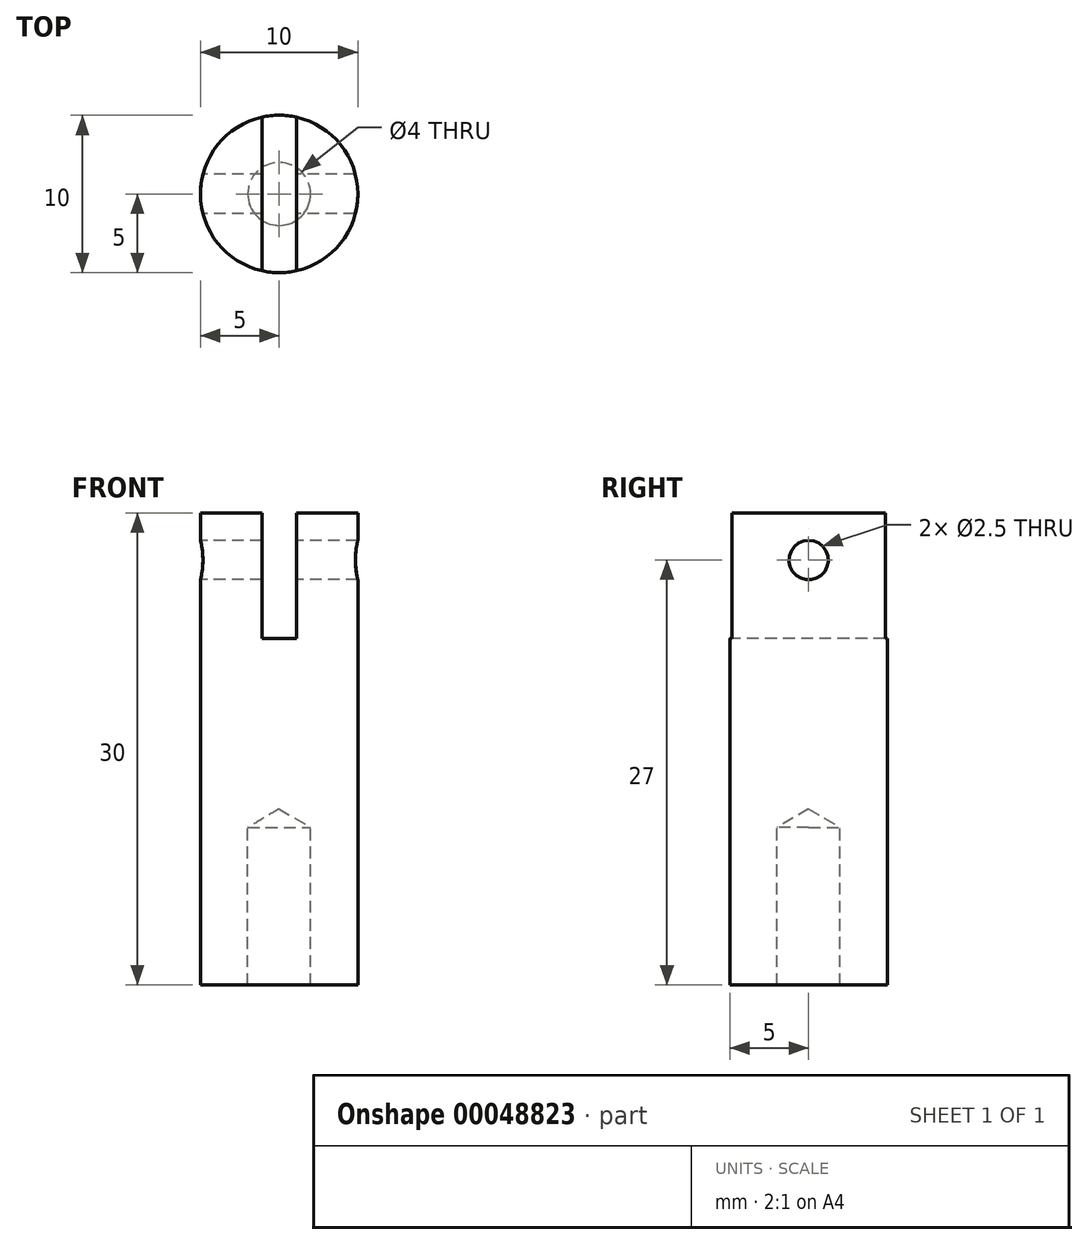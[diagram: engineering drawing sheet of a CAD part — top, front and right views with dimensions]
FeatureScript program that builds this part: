
annotation { "Feature Type Name" : "Feature", "Feature Type Description" : "" }
export const myFeature = defineFeature(function(context is Context, id is Id, definition is map)
    precondition{}
    {
        {
            var Q0;
            Q0=qCreatedBy(makeId("Top.planeOp"),FACE);
            var sketch = newSketch(context, id + "F0", { "sketchPlane" : qUnion([Q0])});
            skCircle(sketch, "E0", {"center": v(0, 0) * mm, "radius": 5 * mm});
            skSolve(sketch);
        }
        {
            var Q0;
            Q0 = qSketchRegion(id + "F0", true);
            extrude(context, id + "F1", {"entities" : qUnion([Q0]), "depth" : 30 * mm});
        }
        {
            var Q0;
            Q0=makeQuery(id+"F1.opExtrude","CAP_FACE",FACE,{"disambiguationData":[OSD([sQuery(id+"F0.wireOp",EDGE,"E0")])],"isStart":false});
            var sketch = newSketch(context, id + "F2", { "sketchPlane" : qUnion([Q0])});
            skLineSegment(sketch, "E1", {"start": v(-1.1, 4.88) * mm, "end": v(-1.1, -4.88) * mm, "construction": true});
            skLineSegment(sketch, "E2.MirrorCS", {"start": v(1.1, 4.88) * mm, "end": v(1.1, -4.88) * mm, "construction": true});
            skLineSegment(sketch, "E3", {"start": v(-1.1, 4.88) * mm, "end": v(-1.1, -4.88) * mm});
            skLineSegment(sketch, "E4", {"start": v(1.1, 4.88) * mm, "end": v(1.1, -4.88) * mm});
            skSolve(sketch);
        }
        {
            var Q0;
            {var subQ0=sQuery(id+"F2.wireOp",EDGE,"E3");Q0=makeQuery(id+"F2.imprint","IMPRINT",FACE,{"disambiguationData":[TD([[makeQuery(id+"F2.imprint","IMPRINT",EDGE,{"derivedFrom":subQ0}),1.0]])]});}
            extrude(context, id + "F3", {"entities" : qUnion([Q0]), "operationType" : NewBodyOperationType.REMOVE, "oppositeDirection" : true, "depth" : 8 * mm});
        }
        {
            var Q0;
            Q0=qCreatedBy(makeId("Right.planeOp"),FACE);
            var sketch = newSketch(context, id + "F4", { "sketchPlane" : qUnion([Q0])});
            skPoint(sketch, "E5", {"position": v(0, 27) * mm});
            skCircle(sketch, "E6", {"center": v(0, 27) * mm, "radius": 1.25 * mm});
            skSolve(sketch);
        }
        {
            var Q0;
            Q0=makeQuery(id+"F4.imprint","IMPRINT",FACE,{"disambiguationData":[TD([[makeQuery(id+"F4.imprint","IMPRINT",EDGE,{"derivedFrom":sQuery(id+"F4.wireOp",EDGE,"E6")}),1.0]])]});
            var Q1;
            Q1=sQuery(id+"F4.wireOp",EDGE,"E6");
            extrude(context, id + "F5", {"entities" : qUnion([Q0]), "operationType" : NewBodyOperationType.REMOVE, "surfaceEntities" : qUnion([Q1]), "depth" : 10 * mm, "symmetric" : true});
        }
        {
            var Q0;
            Q0=makeQuery(id+"F1.opExtrude","CAP_FACE",FACE,{"disambiguationData":[OSD([sQuery(id+"F0.wireOp",EDGE,"E0")])],"isStart":true});
            var sketch = newSketch(context, id + "F6", { "sketchPlane" : qUnion([Q0])});
            skPoint(sketch, "E7", {"position": v(0, 0) * mm});
            skSolve(sketch);
        }
        {
            var Q0;
            Q0=sQuery(id+"F6.wireOp",VERTEX,"E7");
            var Q1;
            Q1=makeQuery(id+"F1.opExtrude","SWEPT_BODY",BODY,{"disambiguationData":[OSD([sQuery(id+"F0.wireOp",EDGE,"E0")])]});
            hole(context, id + "F7", {"style" : HoleStyle.SIMPLE, "endStyle" : HoleEndStyle.BLIND, "standardTappedOrClearance" : lookupTablePath({ "standard" : "ISO", "engagement" : "75%", "pitch" : "1 mm", "size" : "M5", "type" : "Tapped" }), "standardBlindInLast" : lookupTablePath({ "standard" : "ISO", "engagement" : "75%", "pitch" : "1 mm", "size" : "M5", "type" : "Tapped" }), "holeDiameter" : 4 * mm, "holeDepth" : 10 * mm, "locations" : qUnion([Q0]), "scope" : qUnion([Q1]), "startStyle" : HoleStartStyle.PART});
        }
    });
